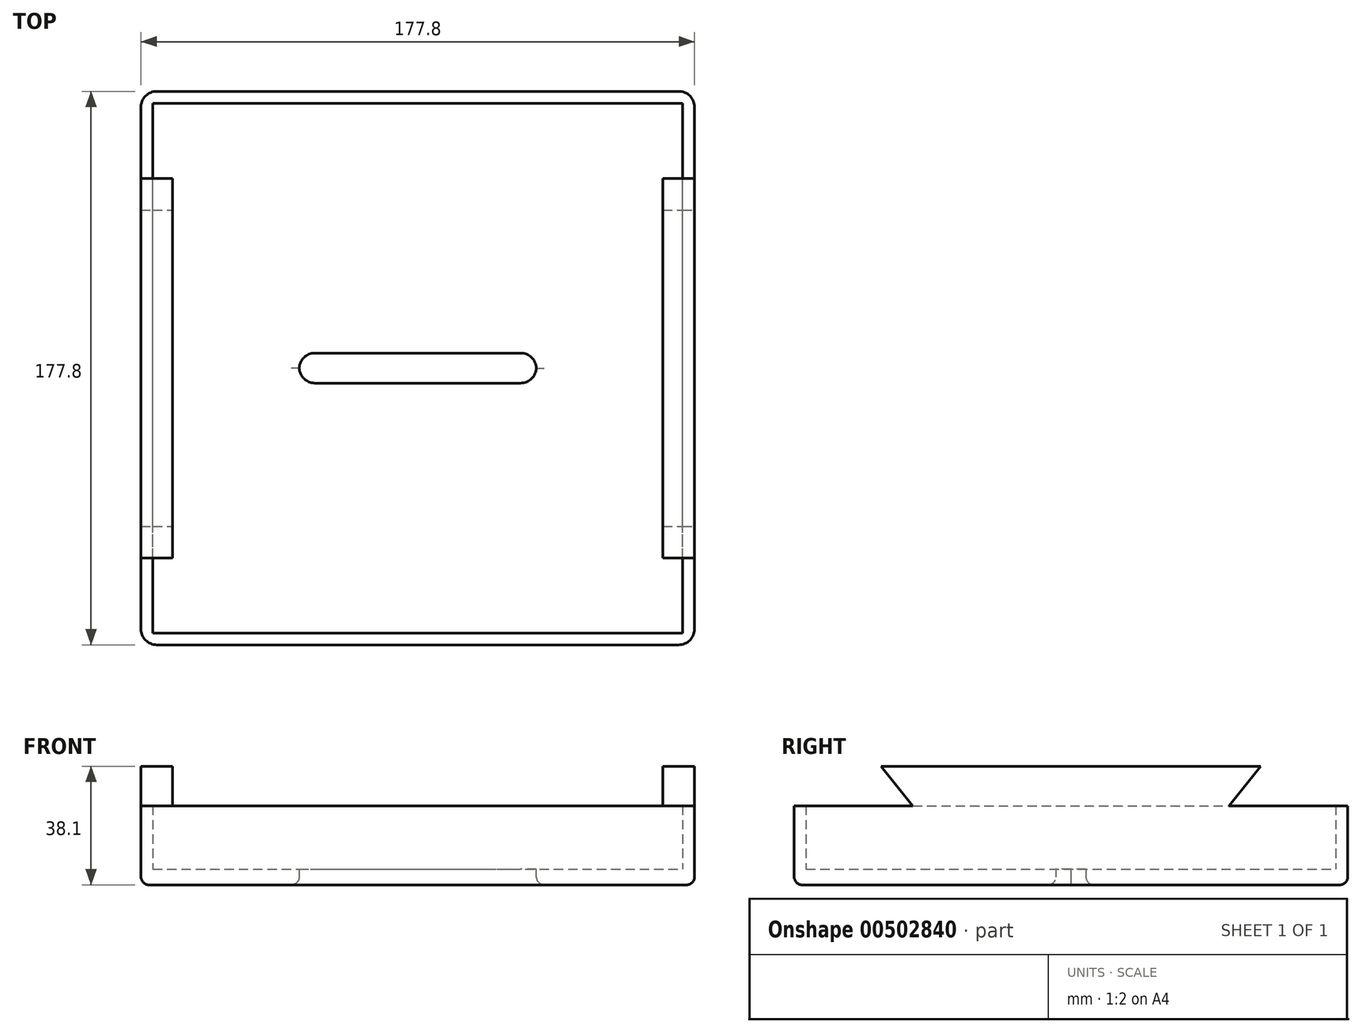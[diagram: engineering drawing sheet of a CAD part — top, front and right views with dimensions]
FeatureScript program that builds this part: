
annotation { "Feature Type Name" : "Feature", "Feature Type Description" : "" }
export const myFeature = defineFeature(function(context is Context, id is Id, definition is map)
    precondition{}
    {
        {
            var Q0;
            Q0=qCreatedBy(makeId("Top.planeOp"),FACE);
            var sketch = newSketch(context, id + "F0", { "sketchPlane" : qUnion([Q0])});
            skLineSegment(sketch, "E0.bottom", {"start": v(88.9, 88.9) * mm, "end": v(-88.9, 88.9) * mm});
            skLineSegment(sketch, "E0.top", {"start": v(88.9, -88.9) * mm, "end": v(-88.9, -88.9) * mm});
            skLineSegment(sketch, "E0.left", {"start": v(88.9, 88.9) * mm, "end": v(88.9, -88.9) * mm});
            skLineSegment(sketch, "E0.right", {"start": v(-88.9, 88.9) * mm, "end": v(-88.9, -88.9) * mm});
            skPoint(sketch, "E0.middle", {"position": v(0, 0) * mm});
            skLineSegment(sketch, "E1.bottom", {"start": v(-85.1, -85.1) * mm, "end": v(85.1, -85.1) * mm});
            skLineSegment(sketch, "E1.top", {"start": v(-85.1, 85.1) * mm, "end": v(85.1, 85.1) * mm});
            skLineSegment(sketch, "E1.left", {"start": v(-85.1, -85.1) * mm, "end": v(-85.1, 85.1) * mm});
            skLineSegment(sketch, "E1.right", {"start": v(85.1, -85.1) * mm, "end": v(85.1, 85.1) * mm});
            skLineSegment(sketch, "E2.bottom", {"start": v(-38.1, 4.83) * mm, "end": v(38.1, 4.83) * mm});
            skLineSegment(sketch, "E2.top", {"start": v(-38.1, -4.83) * mm, "end": v(38.1, -4.83) * mm});
            skLineSegment(sketch, "E2.left", {"start": v(-38.1, 4.83) * mm, "end": v(-38.1, -4.83) * mm});
            skLineSegment(sketch, "E2.right", {"start": v(38.1, 4.83) * mm, "end": v(38.1, -4.83) * mm});
            skSolve(sketch);
        }
        {
            var Q0;
            Q0=makeQuery(id+"F0.imprint","IMPRINT",FACE,{"disambiguationData":[TD([[makeQuery(id+"F0.imprint","IMPRINT",EDGE,{"derivedFrom":sQuery(id+"F0.wireOp",EDGE,"E0.bottom")}),1.0]])]});
            extrude(context, id + "F1", {"entities" : qUnion([Q0]), "depth" : 25.4 * mm});
        }
        {
            var Q0;
            Q0=makeQuery(id+"F0.imprint","IMPRINT",FACE,{"disambiguationData":[TD([[makeQuery(id+"F0.imprint","IMPRINT",EDGE,{"derivedFrom":sQuery(id+"F0.wireOp",EDGE,"E1.bottom")}),1.0]])]});
            extrude(context, id + "F2", {"entities" : qUnion([Q0]), "operationType" : NewBodyOperationType.ADD, "depth" : 5.08 * mm});
        }
        {
            var Q0;
            Q0=makeQuery(id+"F2.opExtrude","SWEPT_EDGE",EDGE,{"disambiguationData":[OSD([sQuery(id+"F0.wireOp",EDGE,"E2.bottom"),sQuery(id+"F0.wireOp",EDGE,"E2.right")])]});
            var Q1;
            Q1=makeQuery(id+"F2.opExtrude","SWEPT_EDGE",EDGE,{"disambiguationData":[OSD([sQuery(id+"F0.wireOp",EDGE,"E2.top"),sQuery(id+"F0.wireOp",EDGE,"E2.right")])]});
            var Q2;
            Q2=makeQuery(id+"F2.opExtrude","SWEPT_EDGE",EDGE,{"disambiguationData":[OSD([sQuery(id+"F0.wireOp",EDGE,"E2.bottom"),sQuery(id+"F0.wireOp",EDGE,"E2.left")])]});
            var Q3;
            Q3=makeQuery(id+"F2.opExtrude","SWEPT_EDGE",EDGE,{"disambiguationData":[OSD([sQuery(id+"F0.wireOp",EDGE,"E2.top"),sQuery(id+"F0.wireOp",EDGE,"E2.left")])]});
            fillet(context, id + "F3", {"entities" : qUnion([Q0, Q1, Q2, Q3]), "radius" : 5.08 * mm, "tangentPropagation" : true, "allowEdgeOverflow" : false});
        }
        {
            var Q0;
            Q0=makeQuery(id+"F1.opExtrude","SWEPT_FACE",FACE,{"disambiguationData":[OSD([sQuery(id+"F0.wireOp",EDGE,"E0.left")])]});
            var sketch = newSketch(context, id + "F4", { "sketchPlane" : qUnion([Q0])});
            skLineSegment(sketch, "E3", {"start": v(0, 25.4) * mm, "end": v(-50.8, 25.4) * mm});
            skLineSegment(sketch, "E4", {"start": v(0, 25.4) * mm, "end": v(50.8, 25.4) * mm});
            skLineSegment(sketch, "E5", {"start": v(0, 25.4) * mm, "end": v(0, 38.1) * mm});
            skLineSegment(sketch, "E6", {"start": v(0, 38.1) * mm, "end": v(-60.96, 38.1) * mm});
            skLineSegment(sketch, "E7", {"start": v(0, 38.1) * mm, "end": v(60.96, 38.1) * mm});
            skLineSegment(sketch, "E8", {"start": v(60.96, 38.1) * mm, "end": v(50.8, 25.4) * mm});
            skLineSegment(sketch, "E9", {"start": v(-60.96, 38.1) * mm, "end": v(-50.8, 25.4) * mm});
            skSolve(sketch);
        }
        {
            var Q0;
            Q0=makeQuery(id+"F4.imprint","IMPRINT",FACE,{"disambiguationData":[TD([[makeQuery(id+"F4.imprint","IMPRINT",EDGE,{"derivedFrom":sQuery(id+"F4.wireOp",EDGE,"E3")}),-1.0]])]});
            var Q1;
            Q1=makeQuery(id+"F4.imprint","IMPRINT",FACE,{"disambiguationData":[TD([[makeQuery(id+"F4.imprint","IMPRINT",EDGE,{"derivedFrom":sQuery(id+"F4.wireOp",EDGE,"E4")}),-1.0]])]});
            var Q2;
            Q2=makeQuery(id+"F1.opExtrude","SWEPT_FACE",FACE,{"disambiguationData":[OSD([sQuery(id+"F0.wireOp",EDGE,"E0.right")])]});
            extrude(context, id + "F5", {"entities" : qUnion([Q0, Q1]), "operationType" : NewBodyOperationType.ADD, "endBound" : BoundingType.UP_TO_SURFACE, "oppositeDirection" : true, "endBoundEntityFace" : qUnion([Q2]), "depth" : 25.4 * mm});
        }
        {
            var Q0;
            Q0=makeQuery(id+"F1.opExtrude","SWEPT_FACE",FACE,{"disambiguationData":[OSD([sQuery(id+"F0.wireOp",EDGE,"E0.bottom")])]});
            var sketch = newSketch(context, id + "F6", { "sketchPlane" : qUnion([Q0])});
            skLineSegment(sketch, "E10", {"start": v(0, 25.4) * mm, "end": v(-78.74, 25.4) * mm});
            skLineSegment(sketch, "E11", {"start": v(0, 25.4) * mm, "end": v(78.74, 25.4) * mm});
            skLineSegment(sketch, "E12", {"start": v(0, 25.4) * mm, "end": v(0, 40.92) * mm});
            skLineSegment(sketch, "E13", {"start": v(0, 40.92) * mm, "end": v(-78.74, 40.92) * mm});
            skLineSegment(sketch, "E14", {"start": v(-78.74, 40.92) * mm, "end": v(-78.74, 25.4) * mm});
            skLineSegment(sketch, "E15", {"start": v(0, 40.92) * mm, "end": v(78.74, 40.92) * mm});
            skLineSegment(sketch, "E16", {"start": v(78.74, 40.92) * mm, "end": v(78.74, 25.4) * mm});
            skSolve(sketch);
        }
        {
            var Q0;
            Q0=makeQuery(id+"F6.imprint","IMPRINT",FACE,{"disambiguationData":[TD([[makeQuery(id+"F6.imprint","IMPRINT",EDGE,{"derivedFrom":sQuery(id+"F6.wireOp",EDGE,"E10")}),1.0]])]});
            var Q1;
            Q1=makeQuery(id+"F6.imprint","IMPRINT",FACE,{"disambiguationData":[TD([[makeQuery(id+"F6.imprint","IMPRINT",EDGE,{"derivedFrom":sQuery(id+"F6.wireOp",EDGE,"E11")}),1.0]])]});
            extrude(context, id + "F7", {"entities" : qUnion([Q0, Q1]), "operationType" : NewBodyOperationType.REMOVE, "endBound" : BoundingType.THROUGH_ALL, "oppositeDirection" : true, "depth" : 25.4 * mm});
        }
        {
            var Q0;
            Q0=makeQuery(id+"F1.opExtrude","SWEPT_EDGE",EDGE,{"disambiguationData":[OSD([sQuery(id+"F0.wireOp",EDGE,"E0.top"),sQuery(id+"F0.wireOp",EDGE,"E0.left")])]});
            var Q1;
            Q1=makeQuery(id+"F1.opExtrude","SWEPT_EDGE",EDGE,{"disambiguationData":[OSD([sQuery(id+"F0.wireOp",EDGE,"E0.bottom"),sQuery(id+"F0.wireOp",EDGE,"E0.left")])]});
            var Q2;
            Q2=makeQuery(id+"F1.opExtrude","SWEPT_EDGE",EDGE,{"disambiguationData":[OSD([sQuery(id+"F0.wireOp",EDGE,"E0.bottom"),sQuery(id+"F0.wireOp",EDGE,"E0.right")])]});
            var Q3;
            Q3=makeQuery(id+"F1.opExtrude","SWEPT_EDGE",EDGE,{"disambiguationData":[OSD([sQuery(id+"F0.wireOp",EDGE,"E0.top"),sQuery(id+"F0.wireOp",EDGE,"E0.right")])]});
            fillet(context, id + "F8", {"entities" : qUnion([Q0, Q1, Q2, Q3]), "radius" : 5.08 * mm, "tangentPropagation" : true, "allowEdgeOverflow" : false});
        }
        {
            var Q0;
            Q0=makeQuery(id+"F1.opExtrude","CAP_EDGE",EDGE,{"disambiguationData":[OSD([sQuery(id+"F0.wireOp",EDGE,"E0.left")])],"isStart":true});
            var Q1;
            Q1=makeQuery(id+"F1.opExtrude","CAP_EDGE",EDGE,{"disambiguationData":[OSD([sQuery(id+"F0.wireOp",EDGE,"E0.bottom")])],"isStart":true});
            var Q2;
            {var subQ0=sQuery(id+"F0.wireOp",EDGE,"E1.right");var subQ1=sQuery(id+"F0.wireOp",EDGE,"E1.left");var subQ2=sQuery(id+"F0.wireOp",EDGE,"E1.top");var subQ3=sQuery(id+"F0.wireOp",EDGE,"E1.bottom");Q2=makeQuery(id+"F2.boolean.opBoolean","MERGE",FACE,{"derivedFrom":[makeQuery(id+"F1.opExtrude","CAP_FACE",FACE,{"disambiguationData":[OSD([sQuery(id+"F0.wireOp",EDGE,"E0.bottom"),sQuery(id+"F0.wireOp",EDGE,"E0.top"),sQuery(id+"F0.wireOp",EDGE,"E0.left"),sQuery(id+"F0.wireOp",EDGE,"E0.right"),subQ3,subQ2,subQ1,subQ0])],"isStart":true}),makeQuery(id+"F2.opExtrude","CAP_FACE",FACE,{"disambiguationData":[OSD([subQ3,subQ2,subQ1,subQ0,sQuery(id+"F0.wireOp",EDGE,"E2.bottom"),sQuery(id+"F0.wireOp",EDGE,"E2.top"),sQuery(id+"F0.wireOp",EDGE,"E2.left"),sQuery(id+"F0.wireOp",EDGE,"E2.right")])],"isStart":true})]});}
            fillet(context, id + "F9", {"entities" : qUnion([Q0, Q1, Q2]), "radius" : 2.54 * mm, "tangentPropagation" : true, "allowEdgeOverflow" : false});
        }
    });
